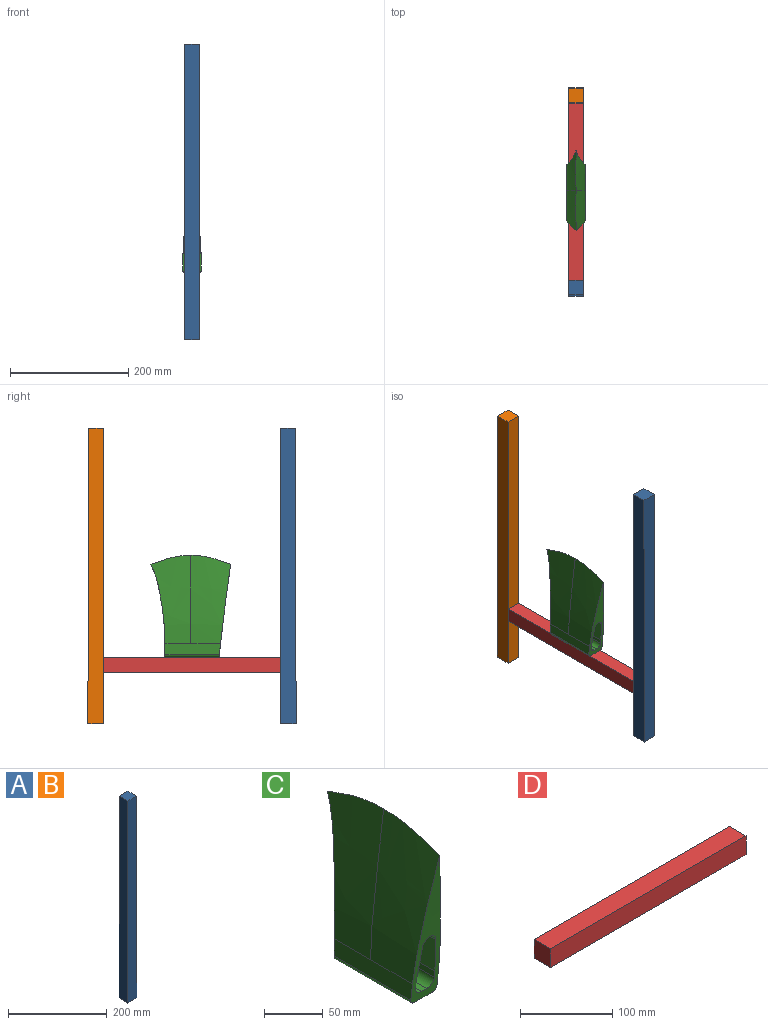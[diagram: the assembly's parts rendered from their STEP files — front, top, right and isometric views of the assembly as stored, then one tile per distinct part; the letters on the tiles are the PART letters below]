
ASSEMBLY  parts=4 mates=3
PART A: 6 faces, bbox 26.2x25x500 mm
  f0: plane 500x25mm, normal (1,0,0), area 12500mm2, adj f1,f3,f4,f5
  f1: plane 25x25mm, normal (0,0,1), area 625mm2, adj f0,f2,f4,f5
  f2: plane 500x25mm, normal (-1,0,0), area 12500mm2, adj f1,f3,f4,f5
  f3: plane 26.16x25mm, normal (0,0,-1), area 653.9mm2, adj f0,f2,f4,f5
  f4: plane 500x26.16mm, normal (0,-1,0), area 12789.4mm2, adj f0,f1,f2,f3
  f5: plane 500x26.16mm, normal (0,1,0), area 12789.4mm2, adj f0,f1,f2,f3
PART B: same geometry as A
PART C: 22 faces, bbox 31.5x134.9x172.5 mm
  f0: plane 100.04x36.7mm, normal (1,0,-0.09), area 3568.7mm2, adj f1,f9,f10,f11
  f1: cylinder r=8mm len=101.6mm, axis (0,-1,0), area 1196.6mm2, adj f0,f2,f10,f11
  f2: plane 101.6x0.14mm, normal (0,0,-1), area 14.2mm2, adj f1,f3,f10,f11
  f3: cylinder r=8mm len=101.6mm, axis (0,-1,0), area 1196.6mm2, adj f2,f4,f10,f11
  f4: plane 100.04x36.7mm, normal (-1,0,-0.09), area 3568.7mm2, adj f3,f5,f10,f11
  f5: plane 94.2x7mm, normal (-1,0,0), area 656.3mm2, adj f4,f6,f10,f11
  f6: cylinder r=8mm len=93.34mm, axis (0,-1,0), area 1167mm2, adj f5,f7,f10,f11
  f7: plane 92.4x6.5mm, normal (0,0,1), area 600.6mm2, adj f6,f8,f10,f11
  f8: cylinder r=8mm len=93.34mm, axis (0,-1,0), area 1167mm2, adj f7,f9,f10,f11
  f9: plane 94.2x7mm, normal (1,0,0), area 656.3mm2, adj f0,f8,f10,f11
  f10: extruded ~156.56x31.5mm, area 2193.6mm2, adj f0,f1,f2,f3,f4,f5,f6,f7
  f11: extruded ~157.31x31.5mm, area 2122.4mm2, adj f0,f1,f2,f3,f4,f5,f6,f7
  f12: bspline ~149.5x67.44mm, area 8640.8mm2, adj f11,f13,f18,f20
  f13: bspline ~149.5x67.44mm, area 8639.1mm2, adj f11,f12,f14,f21
  f14: plane 94.21x18.02mm, normal (1,0,0), area 1676mm2, adj f10,f11,f13,f15,f21
  f15: cylinder r=5mm len=92.06mm, axis (0,-1,0), area 720.8mm2, adj f10,f11,f14,f16
  f16: plane 91.5x21.5mm, normal (0,0,-1), area 1967.2mm2, adj f10,f11,f15,f17
  f17: cylinder r=5mm len=92.06mm, axis (0,-1,0), area 720.8mm2, adj f10,f11,f16,f18
  f18: plane 94.21x18.02mm, normal (-1,0,0), area 1676mm2, adj f10,f11,f12,f17,f20
  f19: plane 0.74x0.21mm, normal (0,1,0), area 0.1mm2, adj f10,f20,f21
  f20: bspline ~149.5x67.44mm, area 7576.8mm2, adj f10,f12,f18,f19,f21
  f21: bspline ~149.5x67.44mm, area 7576.8mm2, adj f10,f13,f14,f19,f20
PART D: 6 faces, bbox 300x25x25 mm
  f0: plane 25x25mm, normal (-1,0,0), area 625mm2, adj f1,f3,f4,f5
  f1: plane 300x25mm, normal (0,0,-1), area 7500mm2, adj f0,f2,f4,f5
  f2: plane 25x25mm, normal (1,0,0), area 625mm2, adj f1,f3,f4,f5
  f3: plane 300x25mm, normal (0,0,1), area 7500mm2, adj f0,f2,f4,f5
  f4: plane 300x25mm, normal (0,-1,0), area 7500mm2, adj f0,f1,f2,f3
  f5: plane 300x25mm, normal (0,1,0), area 7500mm2, adj f0,f1,f2,f3
PLACE A rot(axis=(0,0,-1),90deg) t=(0,-164.5,51.25)mm
PLACE B rot(axis=(0,0,1),90deg) t=(0,160.5,51.25)mm
PLACE C at identity fixed
PLACE D rot(axis=(0,0,-1),90deg) t=(0,-2,-98.24)mm
MATE fastened B.f2 <-> D.f0  axis (0,-1,0) through (0,148,-98.75)mm
MATE fastened D.f2 <-> A.f2  axis (0,-1,0) through (0,-152,-98.75)mm
MATE fastened C.f16 <-> D.f3  axis (0,0,-1) through (0,-2,-86.25)mm
